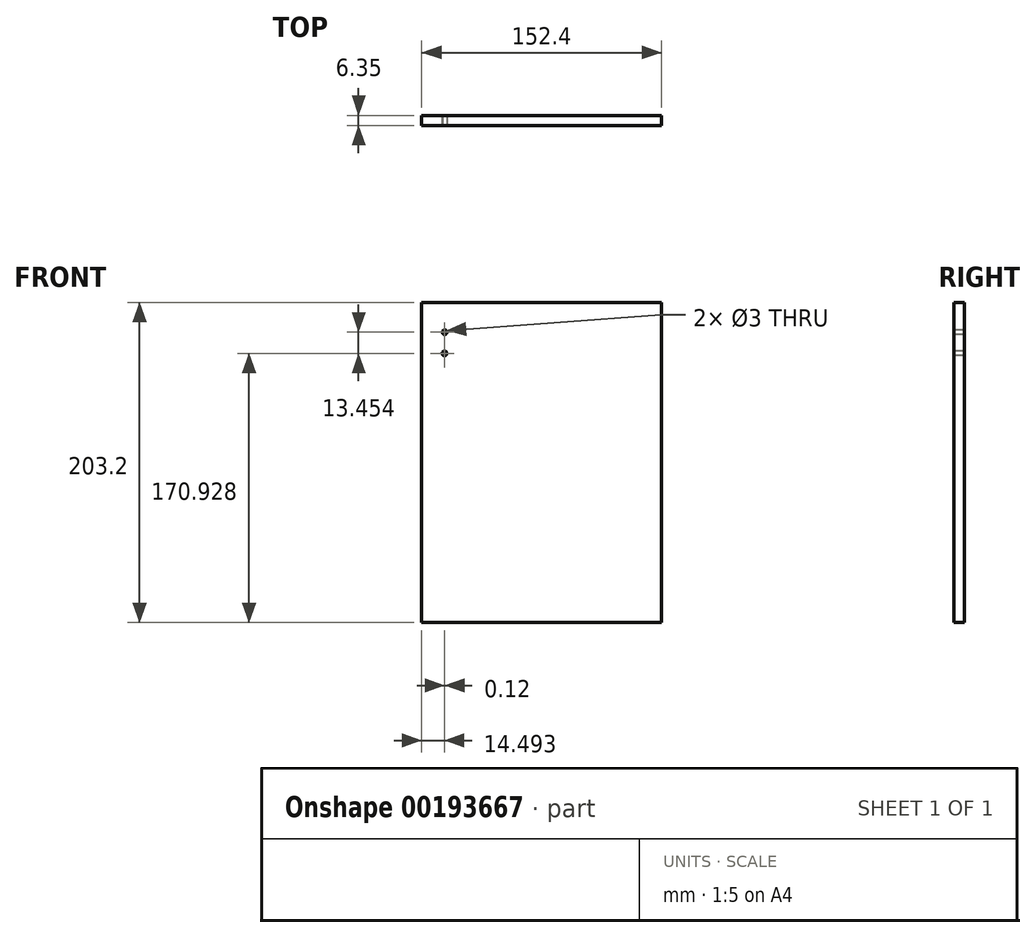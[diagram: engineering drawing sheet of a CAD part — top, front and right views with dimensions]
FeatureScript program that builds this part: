
annotation { "Feature Type Name" : "Feature", "Feature Type Description" : "" }
export const myFeature = defineFeature(function(context is Context, id is Id, definition is map)
    precondition{}
    {
        {
            var Q0;
            Q0=qCreatedBy(makeId("Front.planeOp"),FACE);
            var sketch = newSketch(context, id + "F0", { "sketchPlane" : qUnion([Q0])});
            skLineSegment(sketch, "E0.bottom", {"start": v(-76.2, 101.6) * mm, "end": v(76.2, 101.6) * mm});
            skLineSegment(sketch, "E0.top", {"start": v(-76.2, -101.6) * mm, "end": v(76.2, -101.6) * mm});
            skLineSegment(sketch, "E0.left", {"start": v(-76.2, 101.6) * mm, "end": v(-76.2, -101.6) * mm});
            skLineSegment(sketch, "E0.right", {"start": v(76.2, 101.6) * mm, "end": v(76.2, -101.6) * mm});
            skPoint(sketch, "E0.middle", {"position": v(0, 0) * mm});
            skSolve(sketch);
        }
        {
            var Q0;
            Q0=makeQuery(id+"F0.imprint","IMPRINT",FACE,{"disambiguationData":[TD([[makeQuery(id+"F0.imprint","IMPRINT",EDGE,{"derivedFrom":sQuery(id+"F0.wireOp",EDGE,"E0.bottom")}),-1.0]])]});
            extrude(context, id + "F1", {"entities" : qUnion([Q0]), "depth" : 6.35 * mm});
        }
        {
            var Q0;
            Q0=makeQuery(id+"F1.opExtrude","CAP_FACE",FACE,{"disambiguationData":[OSD([sQuery(id+"F0.wireOp",EDGE,"E0.bottom"),sQuery(id+"F0.wireOp",EDGE,"E0.top"),sQuery(id+"F0.wireOp",EDGE,"E0.left"),sQuery(id+"F0.wireOp",EDGE,"E0.right")])],"isStart":false});
            var sketch = newSketch(context, id + "F2", { "sketchPlane" : qUnion([Q0])});
            skLineSegment(sketch, "E1", {"start": v(-61.54, 101.6) * mm, "end": v(-61.54, 82.55) * mm});
            skLineSegment(sketch, "E2", {"start": v(-61.54, 82.55) * mm, "end": v(-61.54, 69.85) * mm});
            skSolve(sketch);
        }
        {
            var Q0;
            Q0=makeQuery(id+"F2.imprint","IMPRINT",FACE,{"disambiguationData":[TD([[makeQuery(id+"F2.imprint","IMPRINT",EDGE,{"derivedFrom":makeQuery(id+"F1.opExtrude","CAP_EDGE",EDGE,{"disambiguationData":[OSD([sQuery(id+"F0.wireOp",EDGE,"E0.top")])],"isStart":false})}),1.0]])]});
            var sketch = newSketch(context, id + "F3", { "sketchPlane" : qUnion([Q0])});
            skCircle(sketch, "E3", {"center": v(-61.59, 82.78) * mm, "radius": 1.5 * mm});
            skCircle(sketch, "E4", {"center": v(-61.7, 69.33) * mm, "radius": 1.5 * mm});
            skSolve(sketch);
        }
        {
            var Q0;
            Q0=makeQuery(id+"F3.imprint","IMPRINT",FACE,{"disambiguationData":[TD([[makeQuery(id+"F3.imprint","IMPRINT",EDGE,{"derivedFrom":sQuery(id+"F3.wireOp",EDGE,"E3")}),1.0]])]});
            extrude(context, id + "F4", {"entities" : qUnion([Q0]), "operationType" : NewBodyOperationType.REMOVE, "oppositeDirection" : true, "depth" : 25 * mm});
        }
        {
            var Q0;
            Q0=makeQuery(id+"F3.imprint","IMPRINT",FACE,{"disambiguationData":[TD([[makeQuery(id+"F3.imprint","IMPRINT",EDGE,{"derivedFrom":sQuery(id+"F3.wireOp",EDGE,"E4")}),1.0]])]});
            extrude(context, id + "F5", {"entities" : qUnion([Q0]), "operationType" : NewBodyOperationType.REMOVE, "oppositeDirection" : true, "depth" : 25 * mm});
        }
    });
